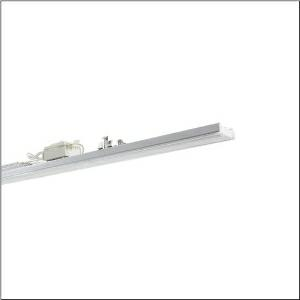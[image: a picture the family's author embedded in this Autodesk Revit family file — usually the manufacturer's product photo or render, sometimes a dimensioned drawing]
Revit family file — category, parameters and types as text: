
# Revit family: licross_11_recessed_ho_51tl12dn455md
name_source: partatom
category: Lighting Fixtures
units: mm (PartAtom-declared; Revit-internal decimal feet)

## family parameters
Cut with Voids When Loaded = No
Host = Face
Light Source = No
Part Type = Normal
Room Calculation Point = No
Round Connector Dimension = Use Diameter
Shared = No

## types (1)
- --- (1 x LED, 900 lm, 5.5 W, 4000K)
    Apparent Load = 6 VA
    CIE Flux Codes = 66 91 98 100 100
    Color Rendering = 80
    Color Temperature = 4000K
    Default Elevation = 1800 mm
    Description = Licross 11 Recessed HO, luminaire insert, of sheet steel, coil coated, white, length: 1.500mm, width: 66mm, height: 67mm, LED rated luminous flux: 5.960lm, light colour: 840, SDCM (Standard Deviation of Colour Matching)MacAdam ≤ 2 SDCM (initial), control gear: DALI 2 (for two DALI lines), with plug, 6-pole, with phase selection, mains connection: 220..240V, AC/DC, 0/50..60Hz, rated input power: 31W, without changeover relay, for emergency light function, for central battery installations according to EN 60598-2-22, internal wiring halogen-free, primary optical cover: cover, of PMMA, light emission: direct distribution, primary light characteristic: symmetric, protection rating (complete): IP40, insulation class (complete): insulation class I (protective earthing), certification: CE, ENEC, VDE, UKCA, protection symbol: D if used in an environment without relevant dust loads with corresponding accessories, impact resistance: IK06, permissible ambient temperature for indoor applications: -25..+45°C, standard: EN 60598-2-22, corresponds to IFS (International Featured Standards) requirements for safety and quality in the food industry, reducing of maximum allowable ambient temperature of 5°C with ceiling mounting, LABS conformity tested according to VDMA 24364:2018-05, The light source and the operating device comply with the requirements of the Ecodesign Regulation (EU) 2019/2020 and are replaceable in accordance with this regulation, packaging unit: 1 piece
    Height = 58 mm
    Lamp = 1 x LED
    Lamp Light Flux = 900 lm
    Lamp Power = 5.5 W
    Lamp count = 1
    Length = 1500 mm
    Luminous efficacy = 164 lm/W
    Manufacturer = Siteco
    ModVariant = No
    Model = 51TL12DN455MD
    Mounting Place = Ceiling
    Mounting Type = Pendant
    Number of Poles = 1
    OnlyDefault = Yes
    Power Factor = 1
    Product Name = Licross 11 Recessed HO
    Product group = luminaire insert | ceiling pendant
    ProductGroupID = 901
    Protection Class = Protection class I
    Protection Degree = IP 40
    RLX_Detail_Level = 1
    RLX_Emergency_Light_Flux = 0 lm
    RLX_Emergency_Type = 0
    RLX_Emergency_Type_DB = No
    RlxData = <blob elided: 24973 chars, md5=06ed5d8c>
    Socket = socket
    Standby Power = 0 W
    System Light Flux = 900 lm
    System Power = 6 W
    Type Comments = : DC mode (central or group accumulator) initial emergency light level
    Type Image = l_1296930.jpg
    URL = http://relux.com
    VarID = @adj_091315
    Voltage = 0 V
    Weight = 0.00 kg
    Width = 66 mm

## geometry (parser evidence)
native form markers: Blend x4, Sweep x9
no freeform markers — native parametric forms only
